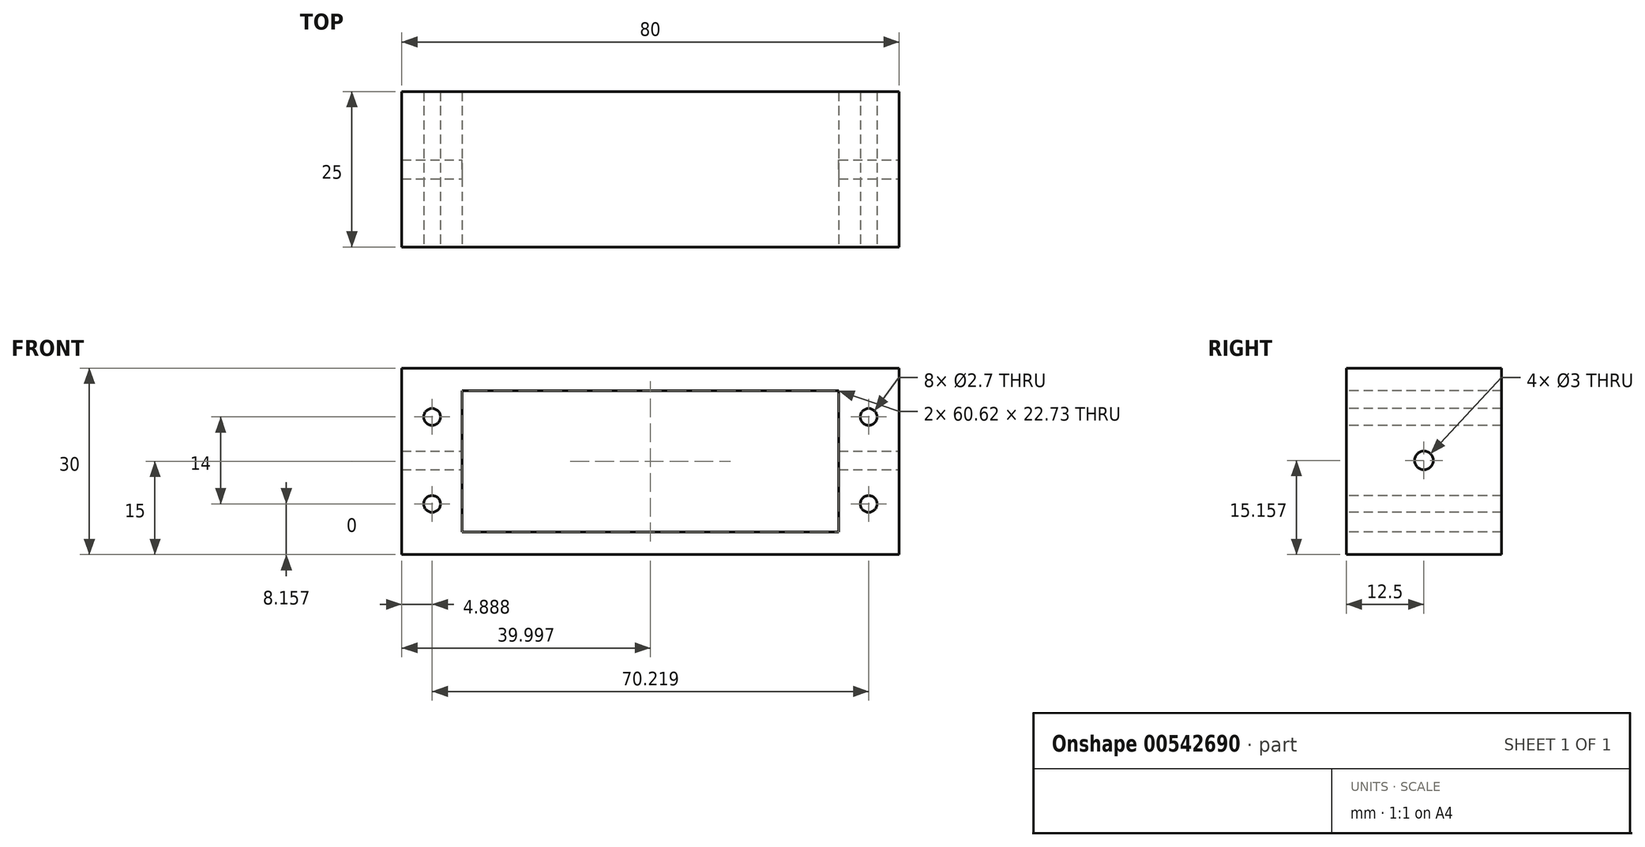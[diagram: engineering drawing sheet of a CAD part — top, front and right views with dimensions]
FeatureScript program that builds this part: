
annotation { "Feature Type Name" : "Feature", "Feature Type Description" : "" }
export const myFeature = defineFeature(function(context is Context, id is Id, definition is map)
    precondition{}
    {
        {
            var Q0;
            Q0=qCreatedBy(makeId("Front.planeOp"),FACE);
            var sketch = newSketch(context, id + "F0", { "sketchPlane" : qUnion([Q0])});
            skLineSegment(sketch, "E0.bottom", {"start": v(-34.84, 30) * mm, "end": v(45.16, 30) * mm});
            skLineSegment(sketch, "E0.top", {"start": v(-34.84, 0) * mm, "end": v(45.16, 0) * mm});
            skLineSegment(sketch, "E0.left", {"start": v(-34.84, 30) * mm, "end": v(-34.84, 0) * mm});
            skLineSegment(sketch, "E0.right", {"start": v(45.16, 30) * mm, "end": v(45.16, 0) * mm});
            skSolve(sketch);
        }
        {
            var Q0;
            Q0=makeQuery(id+"F0.imprint","IMPRINT",FACE,{"disambiguationData":[TD([[makeQuery(id+"F0.imprint","IMPRINT",EDGE,{"derivedFrom":sQuery(id+"F0.wireOp",EDGE,"E0.bottom")}),-1.0]])]});
            extrude(context, id + "F1", {"entities" : qUnion([Q0]), "depth" : 25 * mm, "offsetDistance" : 25 * mm});
        }
        {
            var Q0;
            Q0=makeQuery(id+"F1.opExtrude","CAP_FACE",FACE,{"disambiguationData":[OSD([sQuery(id+"F0.wireOp",EDGE,"E0.bottom"),sQuery(id+"F0.wireOp",EDGE,"E0.top"),sQuery(id+"F0.wireOp",EDGE,"E0.left"),sQuery(id+"F0.wireOp",EDGE,"E0.right")])],"isStart":false});
            var sketch = newSketch(context, id + "F2", { "sketchPlane" : qUnion([Q0])});
            skLineSegment(sketch, "E1", {"start": v(-34.84, 30) * mm, "end": v(45.16, 0) * mm});
            skLineSegment(sketch, "E2", {"start": v(-34.84, 0) * mm, "end": v(45.16, 30) * mm});
            skLineSegment(sketch, "E3.bottom", {"start": v(-25.15, 26.37) * mm, "end": v(35.47, 26.37) * mm});
            skLineSegment(sketch, "E3.top", {"start": v(-25.15, 3.63) * mm, "end": v(35.47, 3.63) * mm});
            skLineSegment(sketch, "E3.left", {"start": v(-25.15, 26.37) * mm, "end": v(-25.15, 3.63) * mm});
            skLineSegment(sketch, "E3.right", {"start": v(35.47, 26.37) * mm, "end": v(35.47, 3.63) * mm});
            skPoint(sketch, "E3.middle", {"position": v(5.16, 15) * mm});
            skSolve(sketch);
        }
        {
            var Q0;
            Q0 = qSketchRegion(id + "F2", true);
            extrude(context, id + "F3", {"entities" : qUnion([Q0]), "operationType" : NewBodyOperationType.REMOVE, "oppositeDirection" : true, "depth" : 20 * mm, "offsetDistance" : 25 * mm});
        }
        {
            var Q0;
            Q0=makeQuery(id+"F1.opExtrude","SWEPT_FACE",FACE,{"disambiguationData":[OSD([sQuery(id+"F0.wireOp",EDGE,"E0.right")])]});
            var sketch = newSketch(context, id + "F4", { "sketchPlane" : qUnion([Q0])});
            skCircle(sketch, "E4", {"center": v(-12.5, 15.16) * mm, "radius": 1.5 * mm});
            skSolve(sketch);
        }
        {
            var Q0;
            Q0=makeQuery(id+"F4.imprint","IMPRINT",FACE,{"disambiguationData":[TD([[makeQuery(id+"F4.imprint","IMPRINT",EDGE,{"derivedFrom":sQuery(id+"F4.wireOp",EDGE,"E4")}),1.0]])]});
            extrude(context, id + "F5", {"entities" : qUnion([Q0]), "operationType" : NewBodyOperationType.REMOVE, "oppositeDirection" : true, "depth" : 1000 * mm, "offsetDistance" : 25 * mm});
        }
        {
            var Q0;
            Q0=makeQuery(id+"F3.boolean.opBoolean","COPY",FACE,{"derivedFrom":makeQuery(id+"F3.opExtrude","CAP_FACE",FACE,{"disambiguationData":[OSD([sQuery(id+"F2.wireOp",EDGE,"E3.bottom"),sQuery(id+"F2.wireOp",EDGE,"E3.top"),sQuery(id+"F2.wireOp",EDGE,"E3.left"),sQuery(id+"F2.wireOp",EDGE,"E3.right")])],"isStart":false})});
            extrude(context, id + "F6", {"entities" : qUnion([Q0]), "operationType" : NewBodyOperationType.REMOVE, "oppositeDirection" : true, "depth" : 25 * mm, "offsetDistance" : 25 * mm});
        }
        {
            var Q0;
            Q0=makeQuery(id+"F1.opExtrude","CAP_FACE",FACE,{"disambiguationData":[OSD([sQuery(id+"F0.wireOp",EDGE,"E0.bottom"),sQuery(id+"F0.wireOp",EDGE,"E0.top"),sQuery(id+"F0.wireOp",EDGE,"E0.left"),sQuery(id+"F0.wireOp",EDGE,"E0.right")])],"isStart":false});
            var sketch = newSketch(context, id + "F7", { "sketchPlane" : qUnion([Q0])});
            skLineSegment(sketch, "E5", {"start": v(-25.15, 0) * mm, "end": v(-25.15, 30) * mm});
            skLineSegment(sketch, "E6", {"start": v(-29.95, 15.16) * mm, "end": v(-29.95, 22.16) * mm});
            skCircle(sketch, "E7", {"center": v(-29.95, 22.16) * mm, "radius": 1.35 * mm});
            skCircle(sketch, "E8.MirrorC", {"center": v(-29.95, 8.16) * mm, "radius": 1.35 * mm});
            skLineSegment(sketch, "E9", {"start": v(35.47, 3.63) * mm, "end": v(35.47, 26.37) * mm});
            skCircle(sketch, "E10.MirrorC", {"center": v(40.27, 8.16) * mm, "radius": 1.35 * mm});
            skCircle(sketch, "E11.MirrorC", {"center": v(40.27, 22.16) * mm, "radius": 1.35 * mm});
            skLineSegment(sketch, "E12", {"start": v(35.47, 26.37) * mm, "end": v(45.16, 30) * mm});
            skLineSegment(sketch, "E13", {"start": v(45.16, 30) * mm, "end": v(40.31, 28.18) * mm});
            skLineSegment(sketch, "E14", {"start": v(5.16, 3.63) * mm, "end": v(5.16, 26.37) * mm});
            skLineSegment(sketch, "E15", {"start": v(5.16, 15) * mm, "end": v(35.47, 15) * mm});
            skCircle(sketch, "E16.MirrorC", {"center": v(-12.66, -18.05) * mm, "radius": 1 * mm});
            skSolve(sketch);
        }
        {
            var Q0;
            Q0 = qSketchRegion(id + "F7", true);
            extrude(context, id + "F8", {"entities" : qUnion([Q0]), "operationType" : NewBodyOperationType.REMOVE, "oppositeDirection" : true, "depth" : 100000 * mm, "offsetDistance" : 25 * mm});
        }
    });
